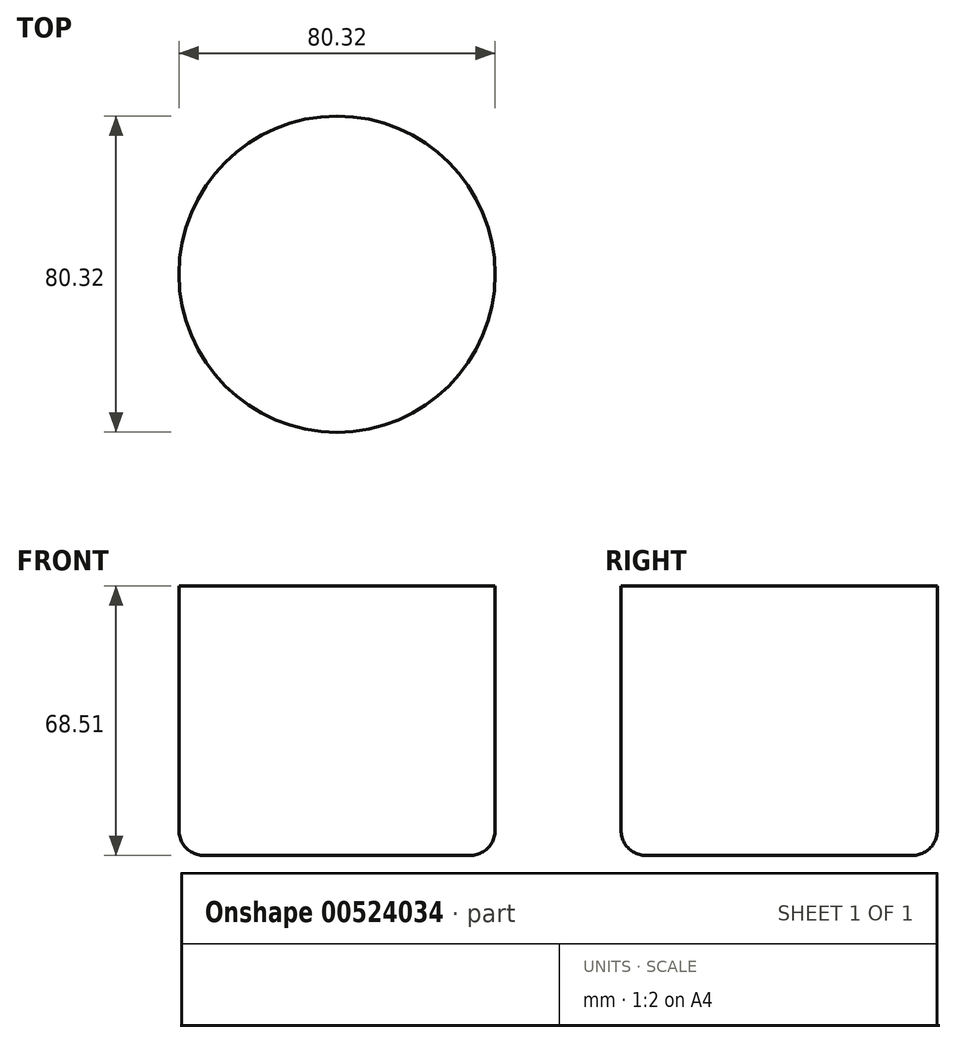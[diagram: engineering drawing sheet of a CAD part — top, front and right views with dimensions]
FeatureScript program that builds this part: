
annotation { "Feature Type Name" : "Feature", "Feature Type Description" : "" }
export const myFeature = defineFeature(function(context is Context, id is Id, definition is map)
    precondition{}
    {
        {
            var Q0;
            Q0=qCreatedBy(makeId("Front.planeOp"),FACE);
            var sketch = newSketch(context, id + "F0", { "sketchPlane" : qUnion([Q0])});
            skLineSegment(sketch, "E0", {"start": v(-43.18, 51.93) * mm, "end": v(-43.18, -10.23) * mm});
            skLineSegment(sketch, "E1", {"start": v(-36.83, -16.58) * mm, "end": v(33.81, -16.58) * mm});
            skLineSegment(sketch, "E2", {"start": v(40.16, -10.23) * mm, "end": v(40.16, 51.93) * mm});
            skLineSegment(sketch, "E3", {"start": v(40.16, 51.93) * mm, "end": v(-43.18, 51.93) * mm});
            skPoint(sketch, "E4.visualSharp", {"position": v(40.16, -16.58) * mm});
            skArc(sketch, "E4.filletArc", {"start": v(33.81, -16.58) * mm, "mid": v(38.3, -14.72) * mm, "end": v(40.16, -10.23) * mm});
            skPoint(sketch, "E5.visualSharp", {"position": v(-43.18, -16.58) * mm});
            skArc(sketch, "E5.filletArc", {"start": v(-43.18, -10.23) * mm, "mid": v(-41.32, -14.72) * mm, "end": v(-36.83, -16.58) * mm});
            skLineSegment(sketch, "E6", {"start": v(0, 0) * mm, "end": v(0, 78.79) * mm});
            skLineSegment(sketch, "E7", {"start": v(0, 90.7) * mm, "end": v(0, -39.12) * mm});
            skSolve(sketch);
        }
        {
            var Q0;
            {var subQ2=sQuery(id+"F0.wireOp",EDGE,"E2");Q0=makeQuery(id+"F0.imprint","IMPRINT",FACE,{"disambiguationData":[TD([[makeQuery(id+"F0.imprint","IMPRINT",EDGE,{"derivedFrom":subQ2}),1.0]])]});}
            var Q1;
            Q1=sQuery(id+"F0.wireOp",EDGE,"E7");
            revolve(context, id + "F1", {"entities" : qUnion([Q0]), "axis" : qUnion([Q1]), "revolveType" : RevolveType.FULL});
        }
    });
